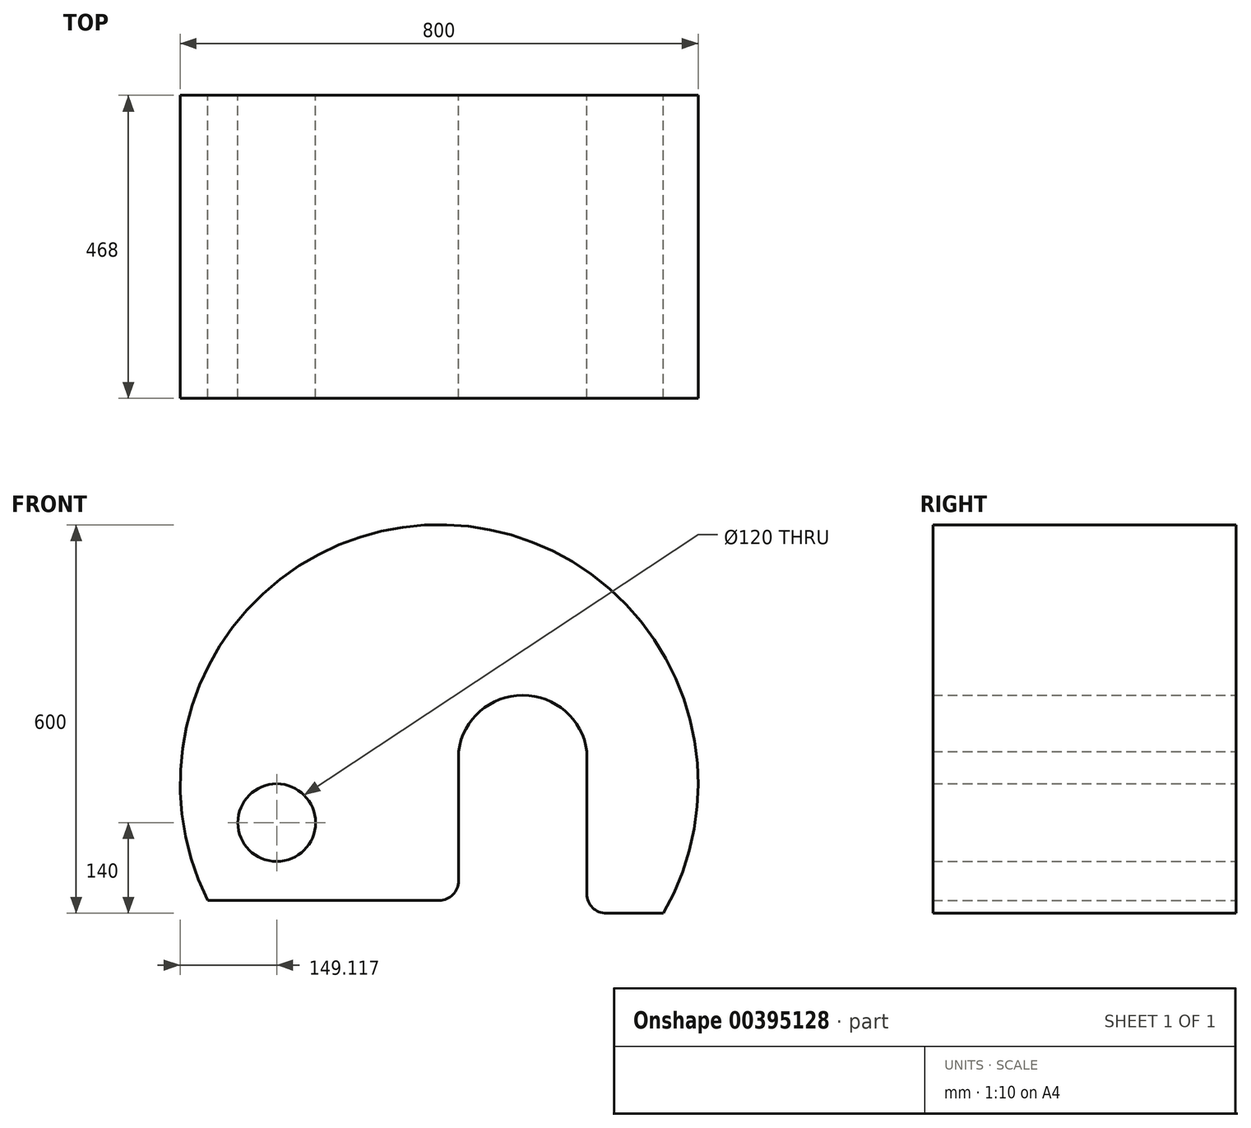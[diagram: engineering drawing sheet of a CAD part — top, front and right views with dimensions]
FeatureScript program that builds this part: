
annotation { "Feature Type Name" : "Feature", "Feature Type Description" : "" }
export const myFeature = defineFeature(function(context is Context, id is Id, definition is map)
    precondition{}
    {
        {
            var Q0;
            Q0=qCreatedBy(makeId("Front.planeOp"),FACE);
            var sketch = newSketch(context, id + "F0", { "sketchPlane" : qUnion([Q0])});
            skArc(sketch, "E0", {"start": v(346.41, -200) * mm, "mid": v(11.37, 399.84) * mm, "end": v(-357.21, -180) * mm});
            skLineSegment(sketch, "E1", {"start": v(0, 495.26) * mm, "end": v(0, 400) * mm, "construction": true});
            skLineSegment(sketch, "E2", {"start": v(30, 0) * mm, "end": v(30, 50) * mm});
            skArc(sketch, "E3", {"start": v(228.23, 50) * mm, "mid": v(129.12, 136.74) * mm, "end": v(30, 50) * mm});
            skLineSegment(sketch, "E4", {"start": v(228.23, 50) * mm, "end": v(228.23, 0) * mm});
            skLineSegment(sketch, "E5", {"start": v(30, 0) * mm, "end": v(30, -150) * mm});
            skLineSegment(sketch, "E6.trimOffspring", {"start": v(0, 0) * mm, "end": v(30, 0) * mm, "construction": true});
            skPoint(sketch, "E7.start.orphan", {"position": v(-605.95, 0) * mm});
            skCircle(sketch, "E8", {"center": v(-250.88, -60) * mm, "radius": 60 * mm});
            skLineSegment(sketch, "E9", {"start": v(228.23, 0) * mm, "end": v(228.23, -170) * mm});
            skArc(sketch, "E10", {"start": v(0, -180) * mm, "mid": v(21.21, -171.21) * mm, "end": v(30, -150) * mm});
            skLineSegment(sketch, "E11", {"start": v(0, -180) * mm, "end": v(-357.21, -180) * mm});
            skLineSegment(sketch, "E12", {"start": v(258.23, -200) * mm, "end": v(346.41, -200) * mm});
            skArc(sketch, "E13", {"start": v(228.23, -170) * mm, "mid": v(237.02, -191.21) * mm, "end": v(258.23, -200) * mm});
            skSolve(sketch);
        }
        {
            var Q0;
            Q0=makeQuery(id+"F0.imprint","IMPRINT",FACE,{"disambiguationData":[TD([[makeQuery(id+"F0.imprint","IMPRINT",EDGE,{"derivedFrom":sQuery(id+"F0.wireOp",EDGE,"E0")}),1.0]])]});
            extrude(context, id + "F1", {"entities" : qUnion([Q0]), "endBound" : BoundingType.SYMMETRIC, "depth" : 468 * mm});
        }
    });
